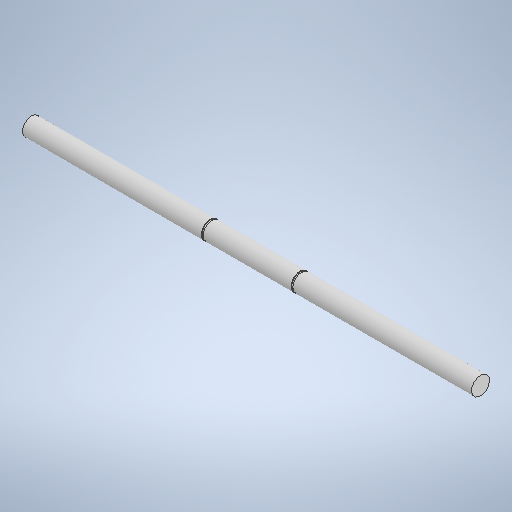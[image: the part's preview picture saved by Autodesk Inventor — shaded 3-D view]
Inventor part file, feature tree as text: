
AUTODESK INVENTOR PART (.ipt)
format: ipt  version: 2025.2 (Build 292293000, 293)  size: 243,200 bytes
history: native  units: mm
features: extrude x2, sketch x1, plane x1, mirror x1
ambient origin geometry x8: Origin, YZ Plane, XZ Plane, XY Plane, X Axis, Y Axis, Z Axis, Center Point
bodies: Solid1 (feature_tree)
feature tree (5):
  sketch  "Sketch1"  dims[d0=5.0mm d1=125.0mm d2=0.0mm d3=0.2mm d6=12.5mm d7=0.5mm d8=0.0mm]
  extrude  "Extrusion1"  Depth=125.0mm TaperAngle=0.0deg
  plane  "Work Plane1"
  extrude  "Extrusion3"  Depth=0.5mm
  mirror  "Mirror1"
